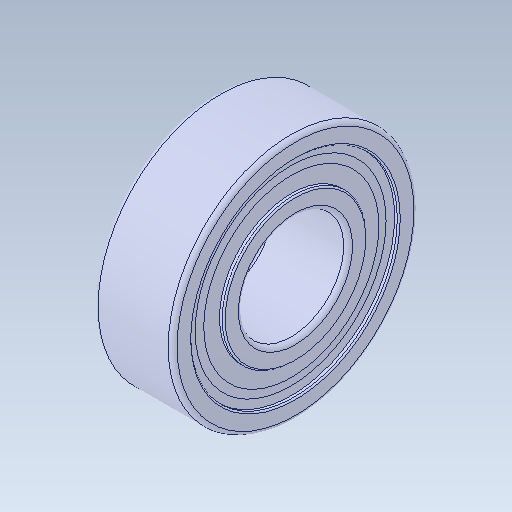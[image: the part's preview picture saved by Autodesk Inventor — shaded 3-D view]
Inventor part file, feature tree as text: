
AUTODESK INVENTOR PART (.ipt)
format: ipt  version: 2020 (Build 240168000, 168)  size: 221,696 bytes
history: native  units: in
note: dims shown in document units (in); Inventor stores cm internally (conversion verified against a paired STEP export)
features: revolve x1
ambient origin geometry x8: Origin, YZ Plane, XZ Plane, XY Plane, X Axis, Y Axis, Z Axis, Center Point
bodies: Solid1 (feature_tree)
feature tree (1):
  revolve  "Revolve1"  [1 undecoded]
note: 1 required parameter value undecoded (feature->parameter linkage not recoverable at this tier; creation-order binding heuristic only, values carry confidence <= 0.55)
